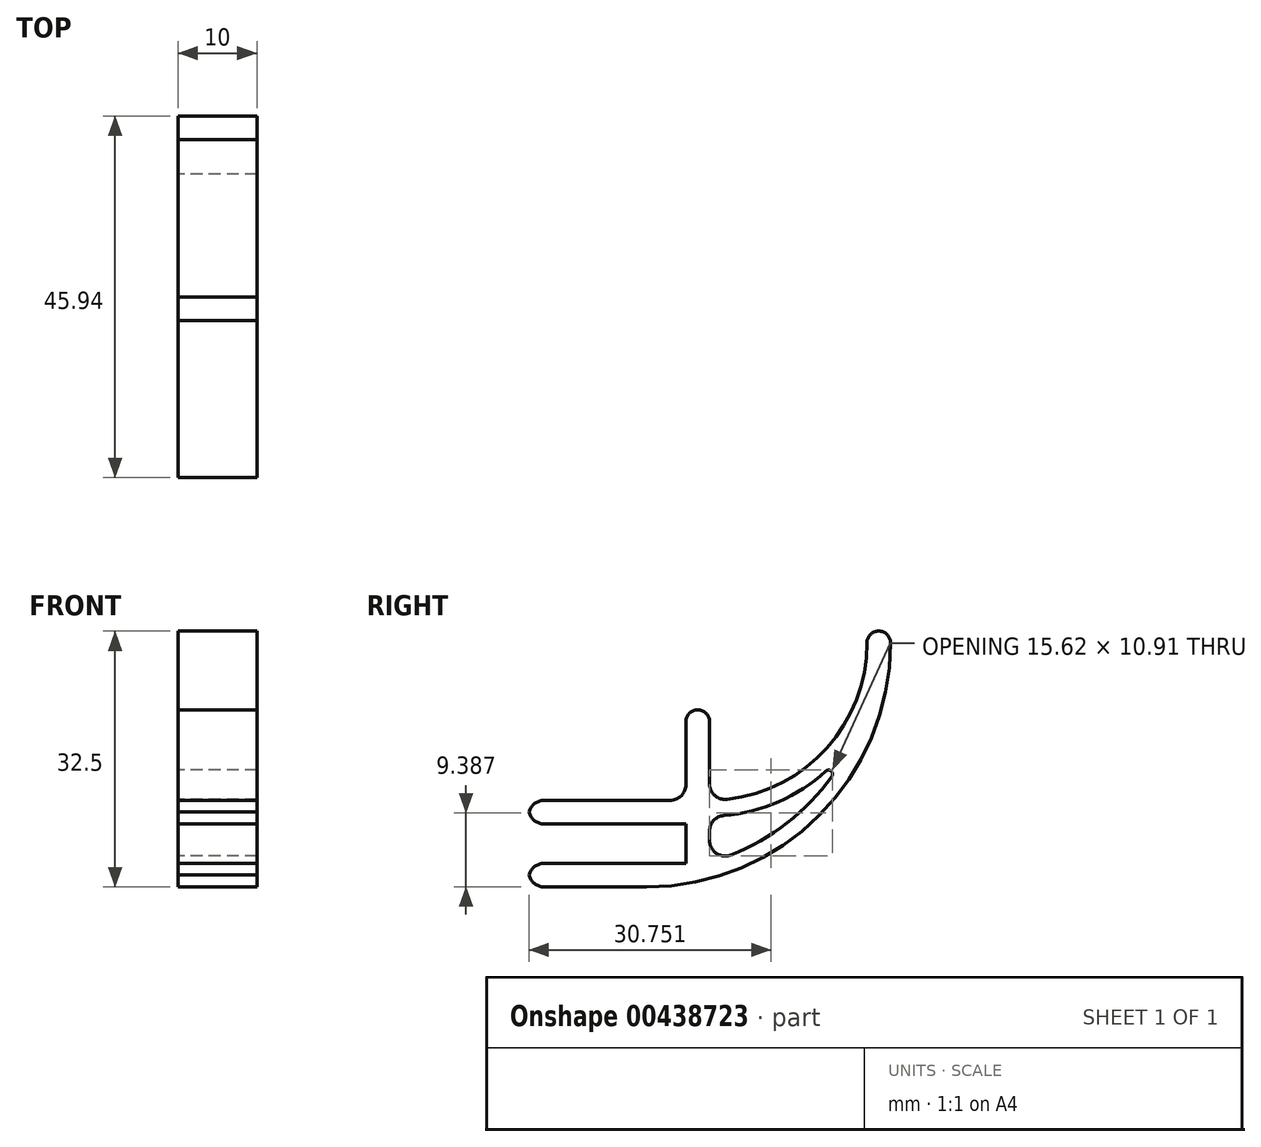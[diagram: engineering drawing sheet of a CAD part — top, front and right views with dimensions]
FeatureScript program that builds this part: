
annotation { "Feature Type Name" : "Feature", "Feature Type Description" : "" }
export const myFeature = defineFeature(function(context is Context, id is Id, definition is map)
    precondition{}
    {
        {
            var Q0;
            Q0=qCreatedBy(makeId("Right.planeOp"),FACE);
            var sketch = newSketch(context, id + "F0", { "sketchPlane" : qUnion([Q0])});
            skLineSegment(sketch, "E0.bottom", {"start": v(0, 0) * mm, "end": v(20, 0) * mm});
            skLineSegment(sketch, "E0.top", {"start": v(0, 5) * mm, "end": v(20, 5) * mm});
            skLineSegment(sketch, "E1.0", {"start": v(0, -3) * mm, "end": v(15, -3) * mm});
            skLineSegment(sketch, "E1.2", {"start": v(0, 8) * mm, "end": v(20, 8) * mm});
            skArc(sketch, "E2", {"start": v(23, 8) * mm, "mid": v(37.14, 13.86) * mm, "end": v(43, 28) * mm});
            skArc(sketch, "E3", {"start": v(46, 28) * mm, "mid": v(44.5, 29.5) * mm, "end": v(43, 28) * mm});
            skArc(sketch, "E4", {"start": v(15, -3) * mm, "mid": v(36.92, 6.08) * mm, "end": v(46, 28) * mm});
            skPoint(sketch, "E5.visualSharp", {"position": v(40.66, 6.58) * mm});
            skLineSegment(sketch, "E6", {"start": v(0, 5) * mm, "end": v(0, 8) * mm});
            skLineSegment(sketch, "E7", {"start": v(0, 0) * mm, "end": v(0, -3) * mm});
            skLineSegment(sketch, "E8", {"start": v(23, 8) * mm, "end": v(23, 18) * mm});
            skLineSegment(sketch, "E9.0", {"start": v(20, 8) * mm, "end": v(20, 18) * mm});
            skArc(sketch, "E10", {"start": v(23, 18) * mm, "mid": v(21.5, 19.5) * mm, "end": v(20, 18) * mm});
            skLineSegment(sketch, "E11", {"start": v(20, 0) * mm, "end": v(20, 5) * mm});
            skArc(sketch, "E12.0", {"start": v(23, 6) * mm, "mid": v(30.93, 7.48) * mm, "end": v(37.79, 11.71) * mm});
            skArc(sketch, "E13.0", {"start": v(23, 0.13) * mm, "mid": v(31.68, 4.28) * mm, "end": v(38.53, 11.05) * mm});
            skLineSegment(sketch, "E14", {"start": v(23, 6) * mm, "end": v(23, 0.13) * mm});
            skPoint(sketch, "E15.visualSharp", {"position": v(41.31, 15.8) * mm});
            skArc(sketch, "E15.filletArc", {"start": v(38.53, 11.05) * mm, "mid": v(38.46, 11.72) * mm, "end": v(37.79, 11.71) * mm});
            skSolve(sketch);
        }
        {
            var Q0;
            Q0 = qSketchRegion(id + "F0", true);
            extrude(context, id + "F1", {"entities" : qUnion([Q0]), "depth" : 10 * mm});
        }
        {
            var Q0;
            Q0=makeQuery(id+"F1.opExtrude","SWEPT_EDGE",EDGE,{"disambiguationData":[OSD([sQuery(id+"F0.wireOp",EDGE,"E1.2"),sQuery(id+"F0.wireOp",EDGE,"E6")])]});
            var Q1;
            Q1=makeQuery(id+"F1.opExtrude","SWEPT_EDGE",EDGE,{"disambiguationData":[OSD([sQuery(id+"F0.wireOp",EDGE,"E0.top"),sQuery(id+"F0.wireOp",EDGE,"E6")])]});
            var Q2;
            Q2=makeQuery(id+"F1.opExtrude","SWEPT_EDGE",EDGE,{"disambiguationData":[OSD([sQuery(id+"F0.wireOp",EDGE,"E0.bottom"),sQuery(id+"F0.wireOp",EDGE,"E7")])]});
            var Q3;
            Q3=makeQuery(id+"F1.opExtrude","SWEPT_EDGE",EDGE,{"disambiguationData":[OSD([sQuery(id+"F0.wireOp",EDGE,"E1.0"),sQuery(id+"F0.wireOp",EDGE,"E7")])]});
            var Q4;
            Q4=makeQuery(id+"F1.opExtrude","SWEPT_EDGE",EDGE,{"disambiguationData":[OSD([sQuery(id+"F0.wireOp",EDGE,"E1.1"),sQuery(id+"F0.wireOp",EDGE,"df83ff71-5bb5-4d22-b546-c743ea21e76c.0")])]});
            var Q5;
            Q5=makeQuery(id+"F1.opExtrude","SWEPT_EDGE",EDGE,{"disambiguationData":[OSD([sQuery(id+"F0.wireOp",EDGE,"E1.1"),sQuery(id+"F0.wireOp",EDGE,"59b5b296-c65b-4319-9280-10f7dd370007.0")])]});
            var Q6;
            Q6=makeQuery(id+"F1.opExtrude","SWEPT_EDGE",EDGE,{"disambiguationData":[OSD([sQuery(id+"F0.wireOp",EDGE,"E1.2"),sQuery(id+"F0.wireOp",EDGE,"E9.0")])]});
            var Q7;
            Q7=makeQuery(id+"F1.opExtrude","SWEPT_EDGE",EDGE,{"disambiguationData":[OSD([sQuery(id+"F0.wireOp",EDGE,"E2"),sQuery(id+"F0.wireOp",EDGE,"E8")])]});
            var Q8;
            Q8=makeQuery(id+"F1.opExtrude","SWEPT_EDGE",EDGE,{"disambiguationData":[OSD([sQuery(id+"F0.wireOp",EDGE,"E12.0"),sQuery(id+"F0.wireOp",EDGE,"E14")])]});
            var Q9;
            Q9=makeQuery(id+"F1.opExtrude","SWEPT_EDGE",EDGE,{"disambiguationData":[OSD([sQuery(id+"F0.wireOp",EDGE,"E13.0"),sQuery(id+"F0.wireOp",EDGE,"E14")])]});
            fillet(context, id + "F2", {"entities" : qUnion([Q0, Q1, Q2, Q3, Q4, Q5, Q6, Q7, Q8, Q9]), "radius" : 2 * mm, "tangentPropagation" : true, "allowEdgeOverflow" : false});
        }
    });
